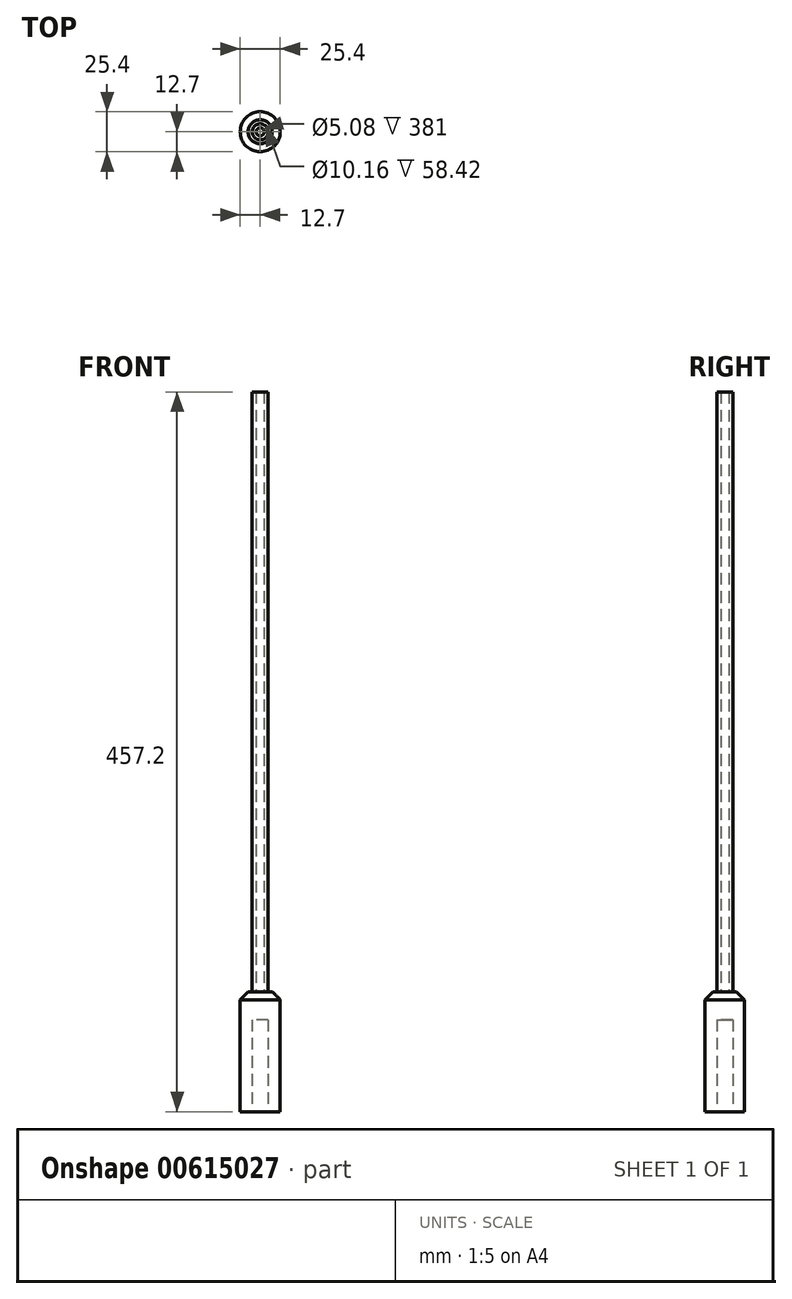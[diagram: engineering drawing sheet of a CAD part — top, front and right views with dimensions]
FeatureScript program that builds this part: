
annotation { "Feature Type Name" : "Feature", "Feature Type Description" : "" }
export const myFeature = defineFeature(function(context is Context, id is Id, definition is map)
    precondition{}
    {
        {
            var Q0;
            Q0=qCreatedBy(makeId("Top.planeOp"),FACE);
            var sketch = newSketch(context, id + "F0", { "sketchPlane" : qUnion([Q0])});
            skCircle(sketch, "E0", {"center": v(0, 0) * mm, "radius": 12.7 * mm});
            skCircle(sketch, "E1", {"center": v(0, 0) * mm, "radius": 5.08 * mm});
            skCircle(sketch, "E2", {"center": v(0, 0) * mm, "radius": 2.54 * mm});
            skSolve(sketch);
        }
        {
            var Q0;
            Q0 = qSketchRegion(id + "F0", true);
            var Q1;
            Q1=makeQuery(id+"F0.imprint","IMPRINT",FACE,{"disambiguationData":[TD([[makeQuery(id+"F0.imprint","IMPRINT",EDGE,{"derivedFrom":sQuery(id+"F0.wireOp",EDGE,"E1")}),1.0]])]});
            var Q2;
            Q2=makeQuery(id+"F0.imprint","IMPRINT",FACE,{"disambiguationData":[TD([[makeQuery(id+"F0.imprint","IMPRINT",EDGE,{"derivedFrom":sQuery(id+"F0.wireOp",EDGE,"E2")}),1.0]])]});
            extrude(context, id + "F1", {"entities" : qUnion([Q0, Q1, Q2]), "depth" : 76.2 * mm, "offsetDistance" : 25.4 * mm});
        }
        {
            var Q0;
            Q0=makeQuery(id+"F0.imprint","IMPRINT",FACE,{"disambiguationData":[TD([[makeQuery(id+"F0.imprint","IMPRINT",EDGE,{"derivedFrom":sQuery(id+"F0.wireOp",EDGE,"E1")}),1.0]])]});
            var Q1;
            Q1=makeQuery(id+"F0.imprint","IMPRINT",FACE,{"disambiguationData":[TD([[makeQuery(id+"F0.imprint","IMPRINT",EDGE,{"derivedFrom":sQuery(id+"F0.wireOp",EDGE,"E2")}),1.0]])]});
            extrude(context, id + "F2", {"entities" : qUnion([Q0, Q1]), "operationType" : NewBodyOperationType.REMOVE, "depth" : 58.42 * mm, "offsetDistance" : 25.4 * mm});
        }
        {
            var Q0;
            Q0=makeQuery(id+"F0.imprint","IMPRINT",FACE,{"disambiguationData":[TD([[makeQuery(id+"F0.imprint","IMPRINT",EDGE,{"derivedFrom":sQuery(id+"F0.wireOp",EDGE,"E1")}),1.0]])]});
            extrude(context, id + "F3", {"entities" : qUnion([Q0]), "operationType" : NewBodyOperationType.ADD, "depth" : 457.2 * mm, "offsetDistance" : 25.4 * mm, "hasSecondDirection" : true, "secondDirectionOppositeDirection" : false, "secondDirectionDepth" : 71.63 * mm});
        }
        {
            var Q0;
            Q0=makeQuery(id+"F1.opExtrude","CAP_EDGE",EDGE,{"disambiguationData":[OSD([sQuery(id+"F0.wireOp",EDGE,"E0")])],"isStart":false});
            chamfer(context, id + "F4", {"entities" : qUnion([Q0]), "width" : 5.08 * mm, "tangentPropagation" : true});
        }
    });
